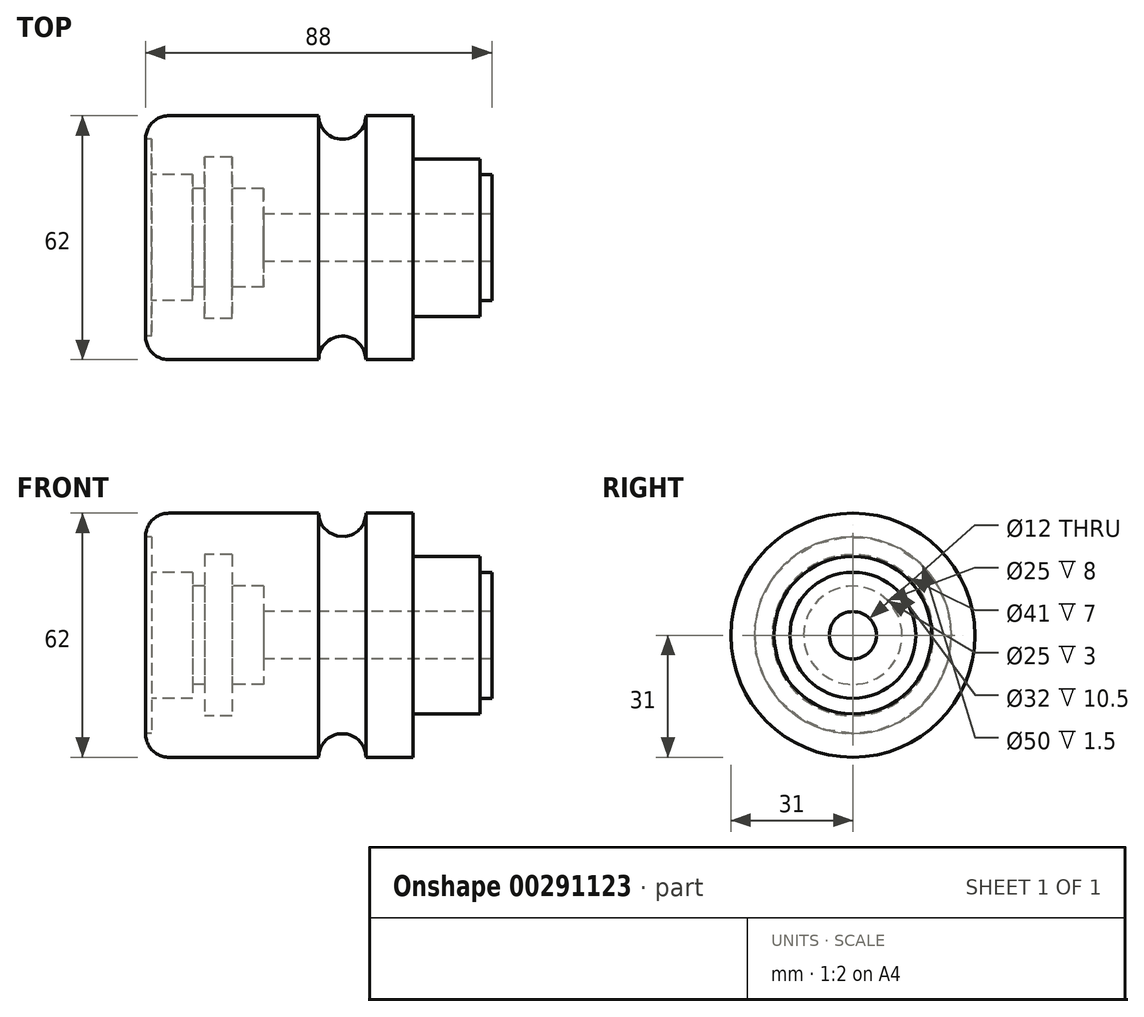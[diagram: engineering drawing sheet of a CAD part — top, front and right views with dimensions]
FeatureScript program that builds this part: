
annotation { "Feature Type Name" : "Feature", "Feature Type Description" : "" }
export const myFeature = defineFeature(function(context is Context, id is Id, definition is map)
    precondition{}
    {
        {
            var Q0;
            Q0=qCreatedBy(makeId("Front.planeOp"),FACE);
            var sketch = newSketch(context, id + "F0", { "sketchPlane" : qUnion([Q0])});
            skLineSegment(sketch, "E0", {"start": v(0, 0) * mm, "end": v(0, 31) * mm});
            skLineSegment(sketch, "E1", {"start": v(0, 31) * mm, "end": v(44, 31) * mm});
            skLineSegment(sketch, "E2", {"start": v(68, 31) * mm, "end": v(68, 20) * mm});
            skLineSegment(sketch, "E3", {"start": v(68, 20) * mm, "end": v(85, 20) * mm});
            skLineSegment(sketch, "E4", {"start": v(85, 20) * mm, "end": v(85, 16) * mm});
            skLineSegment(sketch, "E5", {"start": v(85, 16) * mm, "end": v(88, 16) * mm});
            skLineSegment(sketch, "E6", {"start": v(88, 16) * mm, "end": v(88, 0) * mm});
            skLineSegment(sketch, "E7", {"start": v(88, 0) * mm, "end": v(0, 0) * mm});
            skLineSegment(sketch, "E8", {"start": v(0, 0) * mm, "end": v(-13.1, 0) * mm, "construction": true});
            skArc(sketch, "E9", {"start": v(44, 31) * mm, "mid": v(50, 25) * mm, "end": v(56, 31) * mm});
            skLineSegment(sketch, "E10.trimOffspring", {"start": v(56, 31) * mm, "end": v(68, 31) * mm});
            skSolve(sketch);
        }
        {
            var Q0;
            Q0 = qSketchRegion(id + "F0", true);
            var Q1;
            Q1=sQuery(id+"F0.wireOp",EDGE,"E8");
            revolve(context, id + "F1", {"entities" : qUnion([Q0]), "axis" : qUnion([Q1]), "revolveType" : RevolveType.FULL});
        }
        {
            var Q0;
            Q0=qCreatedBy(makeId("Front.planeOp"),FACE);
            var sketch = newSketch(context, id + "F2", { "sketchPlane" : qUnion([Q0])});
            skLineSegment(sketch, "E11", {"start": v(0, 0) * mm, "end": v(0, 25) * mm});
            skLineSegment(sketch, "E12", {"start": v(0, 25) * mm, "end": v(1.5, 25) * mm});
            skLineSegment(sketch, "E13", {"start": v(1.5, 25) * mm, "end": v(1.5, 16) * mm});
            skLineSegment(sketch, "E14", {"start": v(1.5, 16) * mm, "end": v(12, 16) * mm});
            skLineSegment(sketch, "E15", {"start": v(12, 16) * mm, "end": v(12, 12.5) * mm});
            skLineSegment(sketch, "E16", {"start": v(12, 12.5) * mm, "end": v(15, 12.5) * mm});
            skLineSegment(sketch, "E17", {"start": v(15, 12.5) * mm, "end": v(15, 20.5) * mm});
            skLineSegment(sketch, "E18", {"start": v(15, 20.5) * mm, "end": v(22, 20.5) * mm});
            skLineSegment(sketch, "E19", {"start": v(22, 20.5) * mm, "end": v(22, 12.5) * mm});
            skLineSegment(sketch, "E20", {"start": v(22, 12.5) * mm, "end": v(30, 12.5) * mm});
            skLineSegment(sketch, "E21", {"start": v(30, 12.5) * mm, "end": v(30, 6) * mm});
            skLineSegment(sketch, "E22", {"start": v(30, 6) * mm, "end": v(88, 6) * mm});
            skLineSegment(sketch, "E23", {"start": v(88, 6) * mm, "end": v(88, 0) * mm});
            skLineSegment(sketch, "E24", {"start": v(88, 0) * mm, "end": v(0, 0) * mm});
            skLineSegment(sketch, "E25", {"start": v(0, 0) * mm, "end": v(137.46, 0) * mm, "construction": true});
            skLineSegment(sketch, "E26", {"start": v(0, 0) * mm, "end": v(-52.9, 0) * mm, "construction": true});
            skSolve(sketch);
        }
        {
            var Q0;
            Q0 = qSketchRegion(id + "F2", true);
            var Q1;
            Q1=sQuery(id+"F2.wireOp",EDGE,"E24");
            revolve(context, id + "F3", {"operationType" : NewBodyOperationType.REMOVE, "entities" : qUnion([Q0]), "axis" : qUnion([Q1]), "revolveType" : RevolveType.FULL, "oppositeDirection" : true});
        }
        {
            var Q0;
            Q0=makeQuery(id+"F1.opRevolve","SWEPT_EDGE",EDGE,{"disambiguationData":[OSD([sQuery(id+"F0.wireOp",EDGE,"E0"),sQuery(id+"F0.wireOp",EDGE,"E1")])]});
            fillet(context, id + "F4", {"entities" : qUnion([Q0]), "radius" : 6 * mm, "tangentPropagation" : true, "allowEdgeOverflow" : false});
        }
    });
